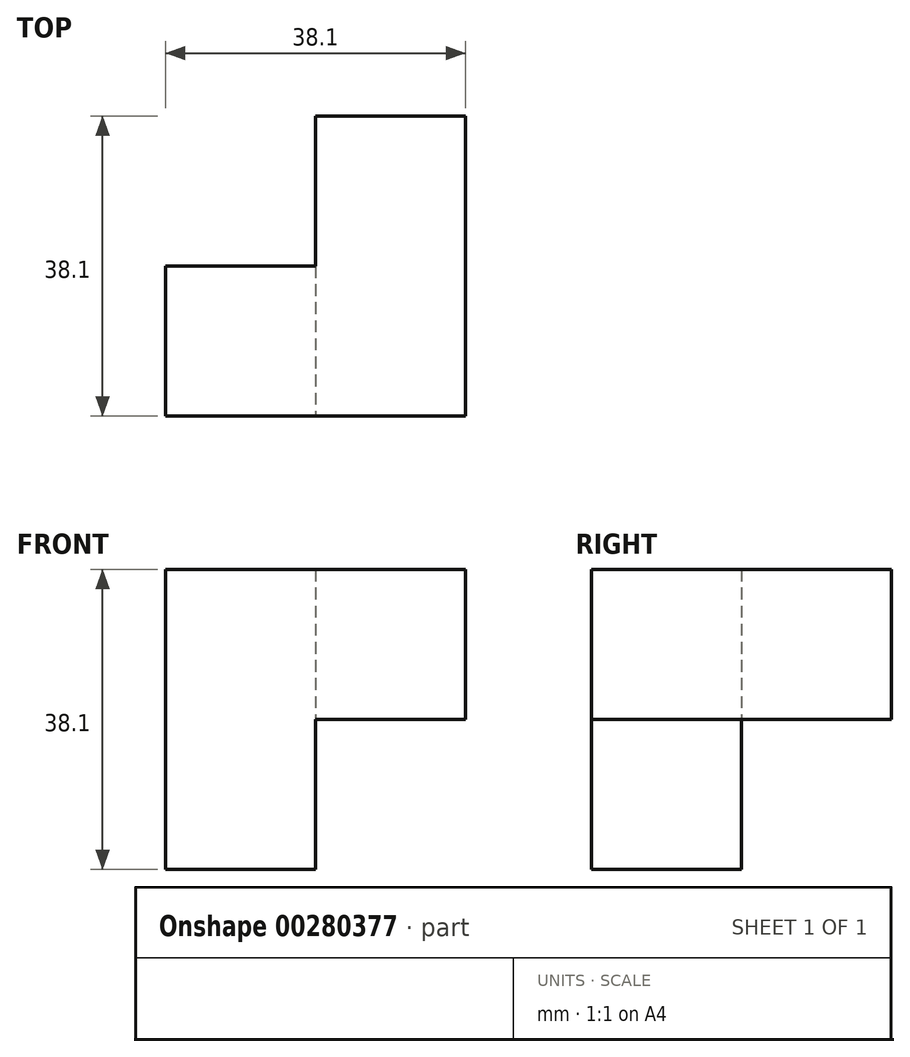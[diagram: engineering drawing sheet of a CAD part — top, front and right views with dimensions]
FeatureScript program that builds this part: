
annotation { "Feature Type Name" : "Feature", "Feature Type Description" : "" }
export const myFeature = defineFeature(function(context is Context, id is Id, definition is map)
    precondition{}
    {
        {
            var Q0;
            Q0=qCreatedBy(makeId("Top.planeOp"),FACE);
            var sketch = newSketch(context, id + "F0", { "sketchPlane" : qUnion([Q0])});
            skLineSegment(sketch, "E0.bottom", {"start": v(0, 0) * mm, "end": v(19.05, 0) * mm});
            skLineSegment(sketch, "E0.top", {"start": v(0, 38.1) * mm, "end": v(19.05, 38.1) * mm});
            skLineSegment(sketch, "E0.left", {"start": v(0, 0) * mm, "end": v(0, 38.1) * mm});
            skLineSegment(sketch, "E0.right", {"start": v(19.05, 0) * mm, "end": v(19.05, 38.1) * mm});
            skLineSegment(sketch, "E1.bottom", {"start": v(0, 19.05) * mm, "end": v(-19.05, 19.05) * mm});
            skLineSegment(sketch, "E1.top", {"start": v(0, 0) * mm, "end": v(-19.05, 0) * mm});
            skLineSegment(sketch, "E1.left", {"start": v(0, 19.05) * mm, "end": v(0, 0) * mm});
            skLineSegment(sketch, "E1.right", {"start": v(-19.05, 19.05) * mm, "end": v(-19.05, 0) * mm});
            skSolve(sketch);
        }
        {
            var Q0;
            Q0 = qSketchRegion(id + "F0", true);
            extrude(context, id + "F1", {"entities" : qUnion([Q0]), "depth" : 19.05 * mm});
        }
        {
            var Q0;
            Q0=makeQuery(id+"F1.opExtrude","CAP_FACE",FACE,{"disambiguationData":[OSD([sQuery(id+"F0.wireOp",EDGE,"E0.bottom"),sQuery(id+"F0.wireOp",EDGE,"E0.top"),sQuery(id+"F0.wireOp",EDGE,"E0.left"),sQuery(id+"F0.wireOp",EDGE,"E0.right"),sQuery(id+"F0.wireOp",EDGE,"E1.bottom"),sQuery(id+"F0.wireOp",EDGE,"E1.top"),sQuery(id+"F0.wireOp",EDGE,"E1.right")])],"isStart":true});
            var sketch = newSketch(context, id + "F2", { "sketchPlane" : qUnion([Q0])});
            skLineSegment(sketch, "E2.bottom", {"start": v(0, -19.05) * mm, "end": v(-19.05, -19.05) * mm});
            skLineSegment(sketch, "E2.top", {"start": v(0, 0) * mm, "end": v(-19.05, 0) * mm});
            skLineSegment(sketch, "E2.left", {"start": v(0, -19.05) * mm, "end": v(0, 0) * mm});
            skLineSegment(sketch, "E2.right", {"start": v(-19.05, -19.05) * mm, "end": v(-19.05, 0) * mm});
            skSolve(sketch);
        }
        {
            var Q0;
            Q0 = qSketchRegion(id + "F2", true);
            extrude(context, id + "F3", {"entities" : qUnion([Q0]), "operationType" : NewBodyOperationType.ADD, "depth" : 19.05 * mm});
        }
    });
